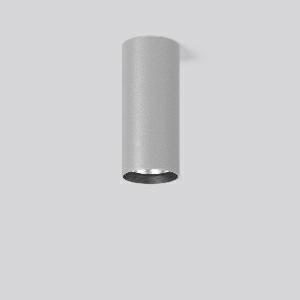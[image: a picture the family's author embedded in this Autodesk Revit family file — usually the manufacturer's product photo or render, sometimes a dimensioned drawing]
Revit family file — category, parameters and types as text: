
# Revit family: heledon_mini_a_931210_004_2_0638
name_source: partatom
category: Lighting Fixtures
units: mm (PartAtom-declared; Revit-internal decimal feet)

## family parameters
Cut with Voids When Loaded = No
Host = Face
Light Source = No
Part Type = Normal
Room Calculation Point = No
Round Connector Dimension = Use Diameter
Shared = No

## types (1)
- HELEDON mini A (1 x LED Modul 927, 3500 lm, 2700)
    Apparent Load = 29 VA
    Approval mark = CE
    CIE Flux Codes = 95 99 100 100 100
    Color Rendering = 92
    Color Temperature = 2700
    Default Elevation = 1800 mm
    Description = Series: HELEDON mini
Cylindrical surface-mounted downlight. Housing: die-cast aluminium, powder-coated. Internal ceiling frame polycarbonate with bayonet mounting. Black plastic ring and recessed LED to prevent glare from the side. Optical assembly with reflector made of MIRO-Silver with 98% total light reflection for outstanding efficiency - can be changed without tools. Best colour rendering index Ra>90. Suitable for Ceiling mounting. Easy installation with a separate ceiling frame with bayonet mounting and plug connection. Driver integrated. Connected via plug-in connector. High quality converter without flickering and stroboscopic effect. The following accessories can be mounted without use of tools: interchangeable lenses, decorative glasses, honeycomb louvre, clear and frosted diffusers, white interchangeable plastic ring. 
Colour: silver
Diameter: 87 mm
Height: 197 mm
Lamp: LED
Socket: without socket
Colour temperature: 2700K
Colour rendering index (CRI): 92
System power: 29 W
Rated luminous flux: 3500 lm
Luminous efficiency: 121 lm/W
Control gear: Regulated power supply
Protection class: I
Type of protection: IP 20
    Height = 197 mm
    Lamp = 1 x LED Modul 927
    Lamp Light Flux = 3500 lm
    Lamp count = 1
    Length = 87 mm
    Lifetime = 50000 h
    Luminous efficacy = 121 lm/W
    Manufacturer = RZB
    ModVariant = No
    Model = 931210.004.2
    Mounting Place = Ceiling
    Mounting Type = Surface mounted
    Number of Poles = 1
    OnlyDefault = Yes
    Power Factor = 1
    Product Name = HELEDON mini A
    Product group = Surface mounted downlights
    ProductGroupID = 302
    Protection Class = Protection class I
    Protection Degree = IP 20
    RLX_Detail_Level = 1
    RLX_Emergency_Light_Flux = 0 lm
    RLX_Emergency_Type = 0
    RLX_Emergency_Type_DB = No
    RlxData = <blob elided: 109285 chars, md5=a253edde>
    Socket = socket
    Standby Power = 0 W
    System Light Flux = 3500 lm
    System Power = 29 W
    Type Comments = Product without accessories
    Type Image = 931188.004.jpg
    URL = http://relux.com
    VarID = ---
    Voltage = 230 V
    Voltage Range = 220-240 V
    Weight = 0.00 kg
    Width = 0 mm  [stored 0 ft]

note: [stored X ft] marks values corroborated as IEEE doubles in the binary element streams (Revit-internal decimal feet)

## geometry (parser evidence)
native form markers: Blend x4, Sweep x8
no freeform markers — native parametric forms only
